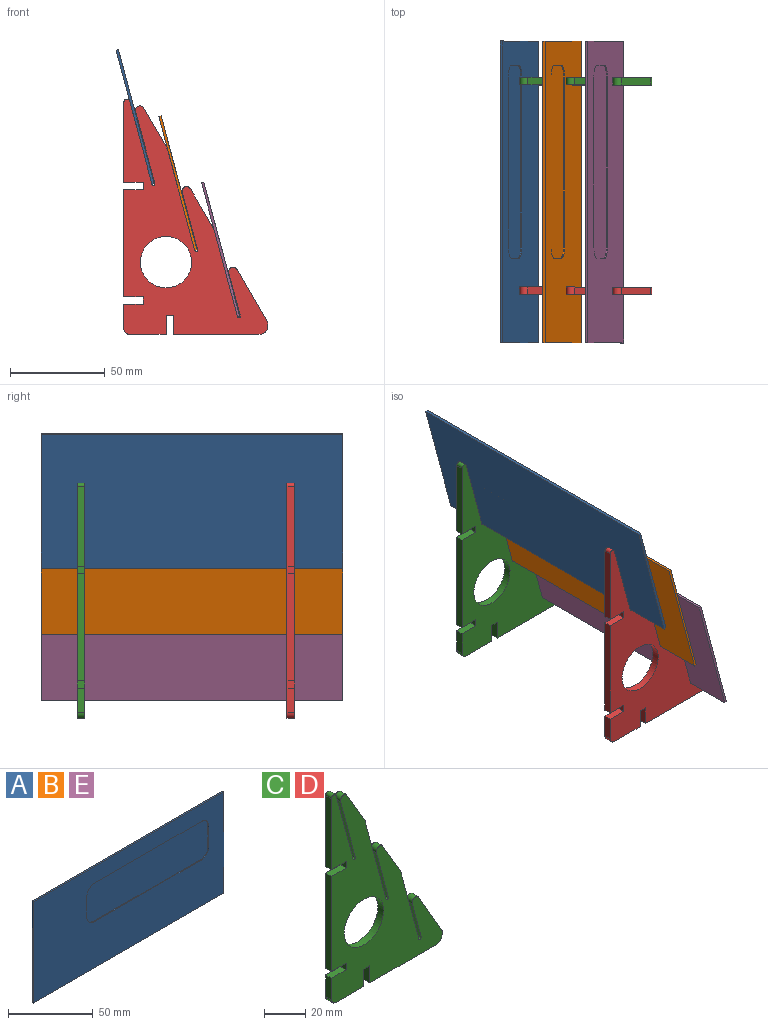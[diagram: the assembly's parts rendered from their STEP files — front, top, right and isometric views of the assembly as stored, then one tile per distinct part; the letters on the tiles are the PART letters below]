
ASSEMBLY  parts=5 mates=4
PART A: 15 faces, bbox 158.8x1.3x73 mm
  f0: plane 73.03x1.27mm, normal (-1,0,0), area 92.7mm2, adj f1,f3,f4,f5
  f1: plane 158.75x1.27mm, normal (0,0,-1), area 201.6mm2, adj f0,f2,f4,f5
  f2: plane 73.03x1.27mm, normal (1,0,0), area 92.7mm2, adj f1,f3,f4,f5
  f3: plane 158.75x1.27mm, normal (0,0,1), area 201.6mm2, adj f0,f2,f4,f5
  f4: plane 158.75x73.03mm, normal (0,1,0), area 11592.7mm2, adj f0,f1,f2,f3
  f5: plane 158.75x73.03mm, normal (0,-1,0), area 8804.8mm2, adj f0,f1,f2,f3,f6,f7,f8,f9
  f6: plane 15.08x0.64mm, normal (-1,0,0), area 9.6mm2, adj f5,f7,f13,f14
  f7: cylinder r=6.35mm len=6.35mm, axis (0,-1,0), area 6.3mm2, adj f5,f6,f8,f14
  f8: plane 88.9x0.64mm, normal (0,0,-1), area 56.5mm2, adj f5,f7,f9,f14
  f9: cylinder r=6.35mm len=6.35mm, axis (0,-1,0), area 6.3mm2, adj f5,f8,f10,f14
  f10: plane 15.08x0.64mm, normal (1,0,0), area 9.6mm2, adj f5,f9,f11,f14
  f11: cylinder r=6.35mm len=6.35mm, axis (0,-1,0), area 6.3mm2, adj f5,f10,f12,f14
  f12: plane 88.9x0.64mm, normal (0,0,1), area 56.5mm2, adj f5,f11,f13,f14
  f13: cylinder r=6.35mm len=6.35mm, axis (0,-1,0), area 6.3mm2, adj f5,f6,f12,f14
  f14: plane 101.6x27.78mm, normal (0,-1,0), area 2788mm2, adj f6,f7,f8,f9,f10,f11,f12,f13
PART B: same geometry as A
PART C: 35 faces, bbox 75.9x4x123.9 mm
  f0: plane 42.19x3.97mm, normal (-1,0,0), area 167.4mm2, adj f1,f31,f33,f34
  f1: plane 10.16x3.97mm, normal (0,0,-1), area 40.3mm2, adj f0,f2,f33,f34
  f2: plane 3.97x3.97mm, normal (-1,0,0), area 15.8mm2, adj f1,f3,f33,f34
  f3: plane 10.16x3.97mm, normal (0,0,1), area 40.3mm2, adj f2,f4,f33,f34
  f4: plane 56.36x3.97mm, normal (-1,0,0), area 223.7mm2, adj f3,f5,f33,f34
  f5: plane 10.16x3.97mm, normal (0,0,-1), area 40.3mm2, adj f4,f6,f33,f34
  f6: plane 3.97x3.97mm, normal (-1,0,0), area 15.8mm2, adj f5,f7,f33,f34
  f7: plane 10.16x3.97mm, normal (0,0,1), area 40.3mm2, adj f6,f8,f33,f34
  f8: plane 12.7x3.97mm, normal (-1,0,0), area 50.4mm2, adj f7,f9,f33,f34
  f9: cylinder r=3.17mm len=3.97mm, axis (0,1,0), area 19.8mm2, adj f8,f10,f33,f34
  f10: plane 19.05x3.97mm, normal (0,0,-1), area 75.6mm2, adj f9,f11,f33,f34
  f11: plane 10.16x3.97mm, normal (1,0,0), area 40.3mm2, adj f10,f12,f33,f34
  f12: plane 3.97x3.97mm, normal (0,0,-1), area 15.8mm2, adj f11,f13,f33,f34
  f13: plane 10.16x3.97mm, normal (-1,0,0), area 40.3mm2, adj f12,f14,f33,f34
  f14: plane 44.93x3.97mm, normal (0,0,-1), area 178.3mm2, adj f13,f15,f33,f34
  f15: cylinder r=4.76mm len=7.14mm, axis (0,1,0), area 39.6mm2, adj f14,f16,f33,f34
  f16: plane 27.03x15.6mm, normal (0.87,0,0.5), area 123.9mm2, adj f15,f17,f33,f34
  f17: cylinder r=2.38mm len=4.44mm, axis (0,1,0), area 27.2mm2, adj f16,f18,f33,f34
  f18: plane 22.63x6.06mm, normal (-0.97,0,-0.26), area 93mm2, adj f17,f19,f33,f34
  f19: cylinder r=0.79mm len=3.97mm, axis (0,1,0), area 9.9mm2, adj f18,f20,f33,f34
  f20: plane 45.83x12.28mm, normal (0.97,0,0.26), area 188.3mm2, adj f19,f21,f33,f34
  f21: plane 21.52x12.42mm, normal (0.87,0,0.5), area 98.6mm2, adj f20,f22,f33,f34
  f22: cylinder r=2.38mm len=4.44mm, axis (0,1,0), area 27.2mm2, adj f21,f23,f33,f34
  f23: plane 30.2x8.09mm, normal (-0.97,0,-0.26), area 124.1mm2, adj f22,f24,f33,f34
  f24: cylinder r=0.79mm len=3.97mm, axis (0,1,0), area 9.9mm2, adj f23,f25,f33,f34
  f25: plane 53.4x14.31mm, normal (0.97,0,0.26), area 219.4mm2, adj f24,f26,f33,f34
  f26: plane 21.52x12.42mm, normal (0.87,0,0.5), area 98.6mm2, adj f25,f27,f33,f34
  f27: cylinder r=2.38mm len=4.44mm, axis (0,1,0), area 27.2mm2, adj f26,f28,f33,f34
  f28: plane 37.77x10.12mm, normal (-0.97,0,-0.26), area 155.2mm2, adj f27,f29,f33,f34
  f29: cylinder r=0.79mm len=3.97mm, axis (0,1,0), area 9.9mm2, adj f28,f30,f33,f34
  f30: plane 43.6x11.68mm, normal (0.97,0,0.26), area 179.1mm2, adj f29,f31,f33,f34
  f31: cylinder r=1.59mm len=3.97mm, axis (0,1,0), area 18.1mm2, adj f0,f30,f33,f34
  f32: cylinder r=13.49mm len=26.99mm, axis (0,1,0), area 336.5mm2, adj f33,f34
  f33: plane 123.94x75.89mm, normal (0,-1,0), area 4375.6mm2, adj f0,f1,f2,f3,f4,f5,f6,f7
  f34: plane 123.94x75.89mm, normal (0,1,0), area 4375.6mm2, adj f0,f1,f2,f3,f4,f5,f6,f7
PART D: same geometry as C
PART E: same geometry as A
PLACE A rot(axis=(-0.13,-0.13,0.98),91deg) t=(16.03,-139.7,79.5)mm
PLACE B rot(axis=(-0.13,-0.13,0.98),91deg) t=(38.54,-139.7,44.57)mm
PLACE C at identity fixed
PLACE D t=(0,-110.33,0)mm
PLACE E rot(axis=(-0.13,-0.13,0.98),91deg) t=(61.04,-139.7,9.65)mm
MATE fastened D.f30 <-> A.f4  axis (0.97,0,0.26) through (14.8,-114.3,79.17)mm
MATE fastened D.f25 <-> B.f4  axis (0.97,0,0.26) through (37.31,-114.3,44.24)mm
MATE fastened E.f4 <-> D.f20  axis (-0.97,0,-0.26) through (59.82,-139.7,9.32)mm
MATE fastened D.f32 <-> C.f32  axis (0,-1,0) through (22.22,-114.3,38.1)mm
